# Revit family: SA Series
name_source: partatom
category: Acessórios do tubo
units: mm (PartAtom-declared; Revit-internal decimal feet)

## family parameters
Com base no plano de trabalho = Não
Compartilhado = Sim
Corte com vazios quando carregada = Não
Cota do conector redondo = Utilizar diâmetro
Número OmniClass = 23.60.30.11.14
Sempre na vertical = Sim
Tipo de parte = Quebra em
Título OmniClass = Pipework Fittings

## types (4) — shared parameters
ESP = 6  [stored 0.019685 ft]
Lookup Table Name = TABELA1
Material = PLÁSTICO
Raio Swing Pipe = 10  [stored 0.0328084 ft]
SupportProjetos: Level of Detail = LOD 300
SupportProjetos: Reviw = R00
zero-valued in all types: Elevação padrão

## per-type parameters (varying)
| type | Descrição | Lenght Swing Pipe | Modelo | RainBird: Code | RainBird: Description |
| SA-6050 | SA6050 - Swing Pipe | 152 | SA6050 | A48030 | SA6050 - Swing Pipe |
| SA-125050 | SA125050 - Swing Pipe | 305 | SA125050 | A48035 | SA125050 - Swing Pipe |
| SA-127575 | SA127575 - Swing Pipe | 305 | SA127575 | A48050 | SA127575 - Swing Pipe |
| SA-185050 | SA185050 - Swing Pipe | 457 | SA185050 | A48065 | SA185050 - Swing Pipe |

note: [stored X ft] marks values corroborated as IEEE doubles in the binary element streams (Revit-internal decimal feet)
